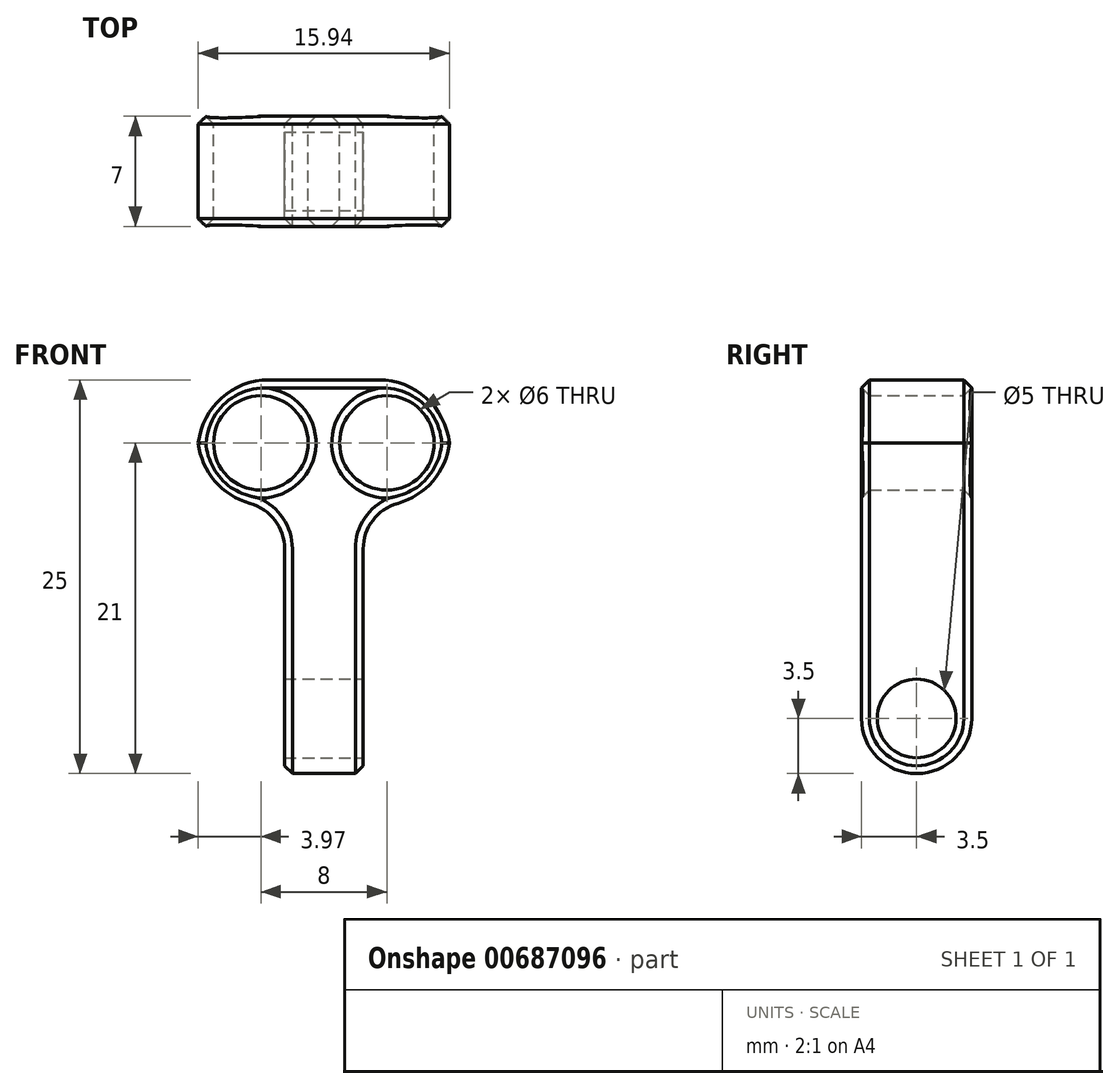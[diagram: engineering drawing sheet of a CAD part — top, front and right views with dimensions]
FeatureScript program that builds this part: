
annotation { "Feature Type Name" : "Feature", "Feature Type Description" : "" }
export const myFeature = defineFeature(function(context is Context, id is Id, definition is map)
    precondition{}
    {
        {
            var Q0;
            Q0=qCreatedBy(makeId("Front.planeOp"),FACE);
            var sketch = newSketch(context, id + "F0", { "sketchPlane" : qUnion([Q0])});
            skLineSegment(sketch, "E0.bottom", {"start": v(2.5, 12.5) * mm, "end": v(-2.5, 12.5) * mm});
            skLineSegment(sketch, "E0.top", {"start": v(2.5, -12.5) * mm, "end": v(-2.5, -12.5) * mm});
            skLineSegment(sketch, "E0.left", {"start": v(2.5, 12.5) * mm, "end": v(2.5, -12.5) * mm});
            skLineSegment(sketch, "E0.right", {"start": v(-2.5, 12.5) * mm, "end": v(-2.5, -12.5) * mm});
            skPoint(sketch, "E0.middle", {"position": v(0, 0) * mm});
            skLineSegment(sketch, "E1.bottom", {"start": v(-8, 12.5) * mm, "end": v(8, 12.5) * mm});
            skLineSegment(sketch, "E1.top", {"start": v(-8, 4.5) * mm, "end": v(8, 4.5) * mm});
            skLineSegment(sketch, "E1.left", {"start": v(-8, 12.5) * mm, "end": v(-8, 4.5) * mm});
            skLineSegment(sketch, "E1.right", {"start": v(8, 12.5) * mm, "end": v(8, 4.5) * mm});
            skCircle(sketch, "E2", {"center": v(-4, 8.5) * mm, "radius": 3 * mm});
            skCircle(sketch, "E3", {"center": v(4, 8.5) * mm, "radius": 3 * mm});
            skSolve(sketch);
        }
        {
            var Q0;
            {var subQ0=sQuery(id+"F0.wireOp",EDGE,"E1.right");Q0=makeQuery(id+"F0.imprint","IMPRINT",FACE,{"disambiguationData":[TD([[makeQuery(id+"F0.imprint","IMPRINT",EDGE,{"derivedFrom":subQ0}),-1.0]])]});}
            var Q1;
            {var subQ3=sQuery(id+"F0.wireOp",EDGE,"E1.left");Q1=makeQuery(id+"F0.imprint","IMPRINT",FACE,{"disambiguationData":[TD([[makeQuery(id+"F0.imprint","IMPRINT",EDGE,{"derivedFrom":subQ3}),1.0]])]});}
            var Q2;
            {var subQ6=sQuery(id+"F0.wireOp",EDGE,"E1.bottom");var subQ8=sQuery(id+"F0.wireOp",EDGE,"E0.left");var subQ12=makeQuery(id+"F0.imprint","INTERSECT",VERTEX,{"derivedFrom":[subQ8,subQ6]});Q2=makeQuery(id+"F0.imprint","IMPRINT",FACE,{"disambiguationData":[TD([[makeQuery(id+"F0.imprint","IMPRINT",EDGE,{"disambiguationData":[TD([[subQ12,-1.0]])],"derivedFrom":subQ8}),-1.0]])]});}
            var Q3;
            {var subQ0=sQuery(id+"F0.wireOp",EDGE,"E0.top");Q3=makeQuery(id+"F0.imprint","IMPRINT",FACE,{"disambiguationData":[TD([[makeQuery(id+"F0.imprint","IMPRINT",EDGE,{"derivedFrom":subQ0}),-1.0]])]});}
            extrude(context, id + "F1", {"entities" : qUnion([Q0, Q1, Q2, Q3]), "depth" : 7 * mm, "offsetDistance" : 25 * mm});
        }
        {
            var Q0;
            Q0=makeQuery(id+"F1.opExtrude","SWEPT_FACE",FACE,{"disambiguationData":[OSD([sQuery(id+"F0.wireOp",EDGE,"E0.left")])]});
            var sketch = newSketch(context, id + "F2", { "sketchPlane" : qUnion([Q0])});
            skCircle(sketch, "E4", {"center": v(-3.5, -9) * mm, "radius": 2.5 * mm});
            skSolve(sketch);
        }
        {
            var Q0;
            Q0=sQuery(id+"F2.wireOp",VERTEX,"E4.center");
            var Q1;
            Q1=makeQuery(id+"F1.opExtrude","SWEPT_BODY",BODY,{"disambiguationData":[OSD([sQuery(id+"F0.wireOp",EDGE,"E0.top"),sQuery(id+"F0.wireOp",EDGE,"E0.left"),sQuery(id+"F0.wireOp",EDGE,"E0.right"),sQuery(id+"F0.wireOp",EDGE,"E1.bottom"),sQuery(id+"F0.wireOp",EDGE,"E1.top"),sQuery(id+"F0.wireOp",EDGE,"E1.left"),sQuery(id+"F0.wireOp",EDGE,"E1.right"),sQuery(id+"F0.wireOp",EDGE,"E2"),sQuery(id+"F0.wireOp",EDGE,"E3")])]});
            hole(context, id + "F3", {"style" : HoleStyle.SIMPLE, "endStyle" : HoleEndStyle.THROUGH, "holeDiameter" : 5 * mm, "majorDiameter" : 5 * mm, "isTappedThrough" : true, "tappedDepth" : 12 * mm, "tapClearance" : 3, "startFromSketch" : true, "locations" : qUnion([Q0]), "scope" : qUnion([Q1])});
        }
        {
            var Q0;
            Q0=makeQuery(id+"F1.opExtrude","SWEPT_EDGE",EDGE,{"disambiguationData":[OSD([sQuery(id+"F0.wireOp",EDGE,"E1.bottom"),sQuery(id+"F0.wireOp",EDGE,"E1.right")])]});
            var Q1;
            Q1=makeQuery(id+"F1.opExtrude","SWEPT_EDGE",EDGE,{"disambiguationData":[OSD([sQuery(id+"F0.wireOp",EDGE,"E1.bottom"),sQuery(id+"F0.wireOp",EDGE,"E1.left")])]});
            var Q2;
            Q2=makeQuery(id+"F1.opExtrude","SWEPT_EDGE",EDGE,{"disambiguationData":[OSD([sQuery(id+"F0.wireOp",EDGE,"E1.top"),sQuery(id+"F0.wireOp",EDGE,"E1.right")])]});
            var Q3;
            Q3=makeQuery(id+"F1.opExtrude","SWEPT_EDGE",EDGE,{"disambiguationData":[OSD([sQuery(id+"F0.wireOp",EDGE,"E1.top"),sQuery(id+"F0.wireOp",EDGE,"E1.left")])]});
            fillet(context, id + "F4", {"entities" : qUnion([Q0, Q1, Q2, Q3]), "radius" : 4.5 * mm, "tangentPropagation" : true, "allowEdgeOverflow" : false});
        }
        {
            var Q0;
            Q0=makeQuery(id+"F1.opExtrude","CAP_EDGE",EDGE,{"disambiguationData":[OSD([sQuery(id+"F0.wireOp",EDGE,"E0.top")])],"isStart":true});
            var Q1;
            Q1=makeQuery(id+"F1.opExtrude","CAP_EDGE",EDGE,{"disambiguationData":[OSD([sQuery(id+"F0.wireOp",EDGE,"E0.top")])],"isStart":false});
            fillet(context, id + "F5", {"entities" : qUnion([Q0, Q1]), "radius" : 3.5 * mm, "tangentPropagation" : true, "allowEdgeOverflow" : false});
        }
        {
            var Q0;
            Q0=makeQuery(id+"F1.opExtrude","SWEPT_EDGE",EDGE,{"disambiguationData":[OSD([sQuery(id+"F0.wireOp",EDGE,"E0.left"),sQuery(id+"F0.wireOp",EDGE,"E1.top")])]});
            var Q1;
            Q1=makeQuery(id+"F1.opExtrude","SWEPT_EDGE",EDGE,{"disambiguationData":[OSD([sQuery(id+"F0.wireOp",EDGE,"E0.right"),sQuery(id+"F0.wireOp",EDGE,"E1.top")])]});
            fillet(context, id + "F6", {"entities" : qUnion([Q0, Q1]), "radius" : 3 * mm, "tangentPropagation" : true, "allowEdgeOverflow" : false});
        }
        {
            var Q0;
            Q0=makeQuery(id+"F1.opExtrude","CAP_EDGE",EDGE,{"disambiguationData":[OSD([sQuery(id+"F0.wireOp",EDGE,"E2")])],"isStart":false});
            var Q1;
            Q1=makeQuery(id+"F1.opExtrude","CAP_EDGE",EDGE,{"disambiguationData":[OSD([sQuery(id+"F0.wireOp",EDGE,"E3")])],"isStart":false});
            var Q2;
            Q2=makeQuery(id+"F3.hole-0.boolean.opBoolean","INTERSECT",EDGE,{"derivedFrom":[makeQuery(id+"F1.opExtrude","SWEPT_FACE",FACE,{"disambiguationData":[OSD([sQuery(id+"F0.wireOp",EDGE,"E0.right")])]}),makeQuery(id+"F3.hole-0.opRevolve","SWEPT_FACE",FACE,{"disambiguationData":[OSD([sQuery(id+"F3.hole-0.sketch.wireOp",EDGE,"core_line_2")])]})]});
            var Q3;
            Q3=makeQuery(id+"F3.hole-0.boolean.opBoolean","COPY",EDGE,{"derivedFrom":makeQuery(id+"F3.hole-0.opRevolve","SWEPT_EDGE",EDGE,{"disambiguationData":[OSD([sQuery(id+"F3.hole-0.sketch.wireOp",EDGE,"core_line_2"),sQuery(id+"F3.hole-0.sketch.wireOp",EDGE,"core_line_3")])]})});
            var Q4;
            Q4=makeQuery(id+"F1.opExtrude","CAP_EDGE",EDGE,{"disambiguationData":[OSD([sQuery(id+"F0.wireOp",EDGE,"E2")])],"isStart":true});
            var Q5;
            Q5=makeQuery(id+"F1.opExtrude","CAP_EDGE",EDGE,{"disambiguationData":[OSD([sQuery(id+"F0.wireOp",EDGE,"E3")])],"isStart":true});
            chamfer(context, id + "F7", {"entities" : qUnion([Q0, Q1, Q2, Q3, Q4, Q5]), "width" : 0.5 * mm, "tangentPropagation" : true});
        }
        {
            var Q0;
            Q0=makeQuery(id+"F1.opExtrude","CAP_EDGE",EDGE,{"disambiguationData":[OSD([sQuery(id+"F0.wireOp",EDGE,"E0.left")])],"isStart":false});
            var Q1;
            Q1=makeQuery(id+"F1.opExtrude","CAP_EDGE",EDGE,{"disambiguationData":[OSD([sQuery(id+"F0.wireOp",EDGE,"E0.right")])],"isStart":false});
            var Q2;
            Q2=makeQuery(id+"F1.opExtrude","CAP_EDGE",EDGE,{"disambiguationData":[OSD([sQuery(id+"F0.wireOp",EDGE,"E1.bottom")])],"isStart":false});
            var Q3;
            Q3=makeQuery(id+"F1.opExtrude","CAP_EDGE",EDGE,{"disambiguationData":[OSD([sQuery(id+"F0.wireOp",EDGE,"E1.bottom")])],"isStart":true});
            chamfer(context, id + "F8", {"entities" : qUnion([Q0, Q1, Q2, Q3]), "width" : 0.5 * mm, "tangentPropagation" : true});
        }
    });
